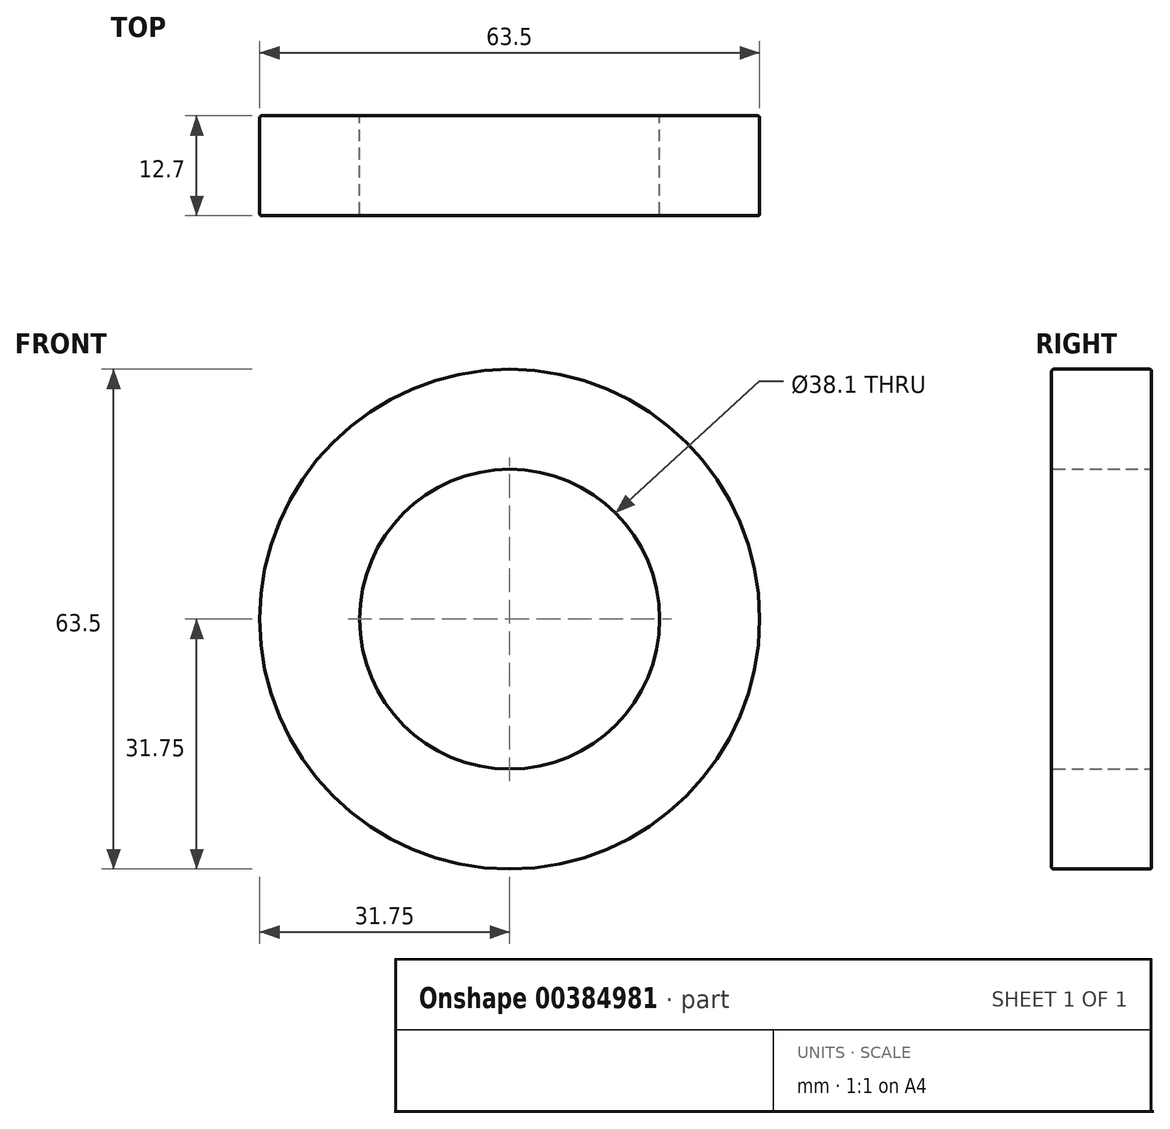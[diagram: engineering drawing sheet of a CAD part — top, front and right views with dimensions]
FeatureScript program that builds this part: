
annotation { "Feature Type Name" : "Feature", "Feature Type Description" : "" }
export const myFeature = defineFeature(function(context is Context, id is Id, definition is map)
    precondition{}
    {
        {
            var Q0;
            Q0=qCreatedBy(makeId("Front.planeOp"),FACE);
            var sketch = newSketch(context, id + "F0", { "sketchPlane" : qUnion([Q0])});
            skCircle(sketch, "E0", {"center": v(0, 0) * mm, "radius": 31.75 * mm});
            skLineSegment(sketch, "E1", {"start": v(-25.4, -19.05) * mm, "end": v(25.4, -19.05) * mm, "construction": true});
            skCircle(sketch, "E2", {"center": v(0, 0) * mm, "radius": 19.05 * mm});
            skSolve(sketch);
        }
        {
            var Q0;
            Q0 = qSketchRegion(id + "F0", true);
            extrude(context, id + "F1", {"entities" : qUnion([Q0]), "depth" : 12.7 * mm});
        }
        {
            var Q0;
            Q0=makeQuery(id+"F1.opExtrude","CAP_EDGE",EDGE,{"disambiguationData":[OSD([sQuery(id+"F0.wireOp",EDGE,"E0")])],"isStart":false});
            var Q1;
            Q1=makeQuery(id+"F1.opExtrude","CAP_EDGE",EDGE,{"disambiguationData":[OSD([sQuery(id+"F0.wireOp",EDGE,"E0")])],"isStart":true});
            var Q2;
            Q2=makeQuery(id+"F1.opExtrude","CAP_EDGE",EDGE,{"disambiguationData":[OSD([sQuery(id+"F0.wireOp",EDGE,"E2")])],"isStart":false});
            var Q3;
            Q3=makeQuery(id+"F1.opExtrude","CAP_EDGE",EDGE,{"disambiguationData":[OSD([sQuery(id+"F0.wireOp",EDGE,"E2")])],"isStart":true});
            fillet(context, id + "F2", {"entities" : qUnion([Q0, Q1, Q2, Q3]), "radius" : 0.25 * mm, "tangentPropagation" : true, "allowEdgeOverflow" : false});
        }
    });
